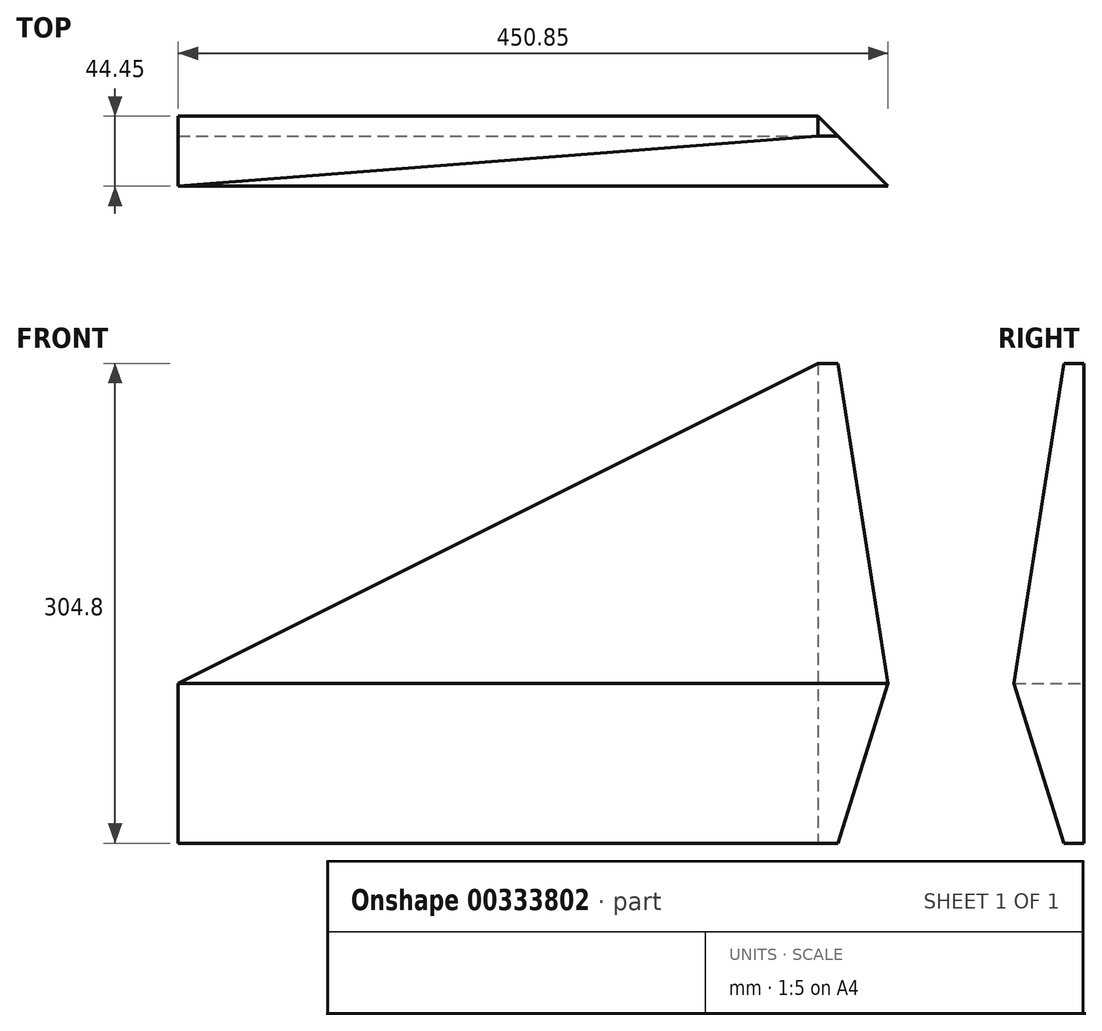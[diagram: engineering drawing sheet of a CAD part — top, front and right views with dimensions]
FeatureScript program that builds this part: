
annotation { "Feature Type Name" : "Feature", "Feature Type Description" : "" }
export const myFeature = defineFeature(function(context is Context, id is Id, definition is map)
    precondition{}
    {
        {
            var Q0;
            Q0=qCreatedBy(makeId("Front.planeOp"),FACE);
            var sketch = newSketch(context, id + "F0", { "sketchPlane" : qUnion([Q0])});
            skLineSegment(sketch, "E0.bottom", {"start": v(-74.09, 0) * mm, "end": v(383.11, 0) * mm});
            skLineSegment(sketch, "E0.top", {"start": v(-74.09, 304.8) * mm, "end": v(383.11, 304.8) * mm});
            skLineSegment(sketch, "E0.left", {"start": v(-74.09, 0) * mm, "end": v(-74.09, 304.8) * mm});
            skLineSegment(sketch, "E0.right", {"start": v(383.11, 0) * mm, "end": v(383.11, 304.8) * mm});
            skSolve(sketch);
        }
        {
            var Q0;
            Q0=qSketchRegion(id+"F0",true);
            extrude(context, id + "F1", {"entities" : qUnion([Q0]), "depth" : 44.45 * mm});
        }
        {
            var Q0;
            Q0=makeQuery(id+"F1.opExtrude","SWEPT_FACE",FACE,{"disambiguationData":[OSD([sQuery(id+"F0.wireOp",EDGE,"E0.right")])]});
            var sketch = newSketch(context, id + "F2", { "sketchPlane" : qUnion([Q0])});
            skLineSegment(sketch, "E1", {"start": v(-12.7, 304.8) * mm, "end": v(-44.45, 101.6) * mm});
            skLineSegment(sketch, "E2", {"start": v(-82.84, 0) * mm, "end": v(-82.84, 304.8) * mm});
            skPoint(sketch, "E2.endSnap0", {"position": v(-22.23, 304.8) * mm});
            skLineSegment(sketch, "E3", {"start": v(-82.84, 304.8) * mm, "end": v(-12.7, 304.8) * mm});
            skLineSegment(sketch, "E4", {"start": v(-44.45, 101.6) * mm, "end": v(-12.7, 0) * mm});
            skLineSegment(sketch, "E5", {"start": v(-12.7, 0) * mm, "end": v(-82.84, 0) * mm});
            skSolve(sketch);
        }
        {
            var Q0;
            Q0=qSketchRegion(id+"F2",true);
            extrude(context, id + "F3", {"entities" : qUnion([Q0]), "operationType" : NewBodyOperationType.REMOVE, "endBound" : BoundingType.THROUGH_ALL, "oppositeDirection" : true, "depth" : 25.4 * mm});
        }
        {
            var Q0;
            Q0=makeQuery(id+"F1.opExtrude","CAP_FACE",FACE,{"disambiguationData":[OSD([sQuery(id+"F0.wireOp",EDGE,"E0.bottom"),sQuery(id+"F0.wireOp",EDGE,"E0.top"),sQuery(id+"F0.wireOp",EDGE,"E0.left"),sQuery(id+"F0.wireOp",EDGE,"E0.right")])],"isStart":true});
            var sketch = newSketch(context, id + "F4", { "sketchPlane" : qUnion([Q0])});
            skLineSegment(sketch, "E6", {"start": v(-332.31, 304.8) * mm, "end": v(74.09, 101.6) * mm});
            skLineSegment(sketch, "E7", {"start": v(74.09, 101.6) * mm, "end": v(74.09, 304.8) * mm});
            skLineSegment(sketch, "E8", {"start": v(74.09, 304.8) * mm, "end": v(-332.31, 304.8) * mm});
            skSolve(sketch);
        }
        {
            var Q0;
            Q0 = qSketchRegion(id + "F4", true);
            extrude(context, id + "F5", {"entities" : qUnion([Q0]), "operationType" : NewBodyOperationType.REMOVE, "endBound" : BoundingType.THROUGH_ALL, "oppositeDirection" : true, "depth" : 25.4 * mm});
        }
        {
            var Q0;
            Q0=makeQuery(id+"F1.opExtrude","SWEPT_FACE",FACE,{"disambiguationData":[OSD([sQuery(id+"F0.wireOp",EDGE,"E0.bottom")])]});
            var sketch = newSketch(context, id + "F6", { "sketchPlane" : qUnion([Q0])});
            skLineSegment(sketch, "E9", {"start": v(383.11, 0) * mm, "end": v(332.31, 0) * mm});
            skLineSegment(sketch, "E10", {"start": v(332.31, 0) * mm, "end": v(383.11, 50.8) * mm});
            skLineSegment(sketch, "E11", {"start": v(383.11, 50.8) * mm, "end": v(383.11, 0) * mm});
            skSolve(sketch);
        }
        {
            var Q0;
            Q0 = qSketchRegion(id + "F6", true);
            extrude(context, id + "F7", {"entities" : qUnion([Q0]), "operationType" : NewBodyOperationType.REMOVE, "endBound" : BoundingType.THROUGH_ALL, "oppositeDirection" : true, "depth" : 25.4 * mm});
        }
    });
